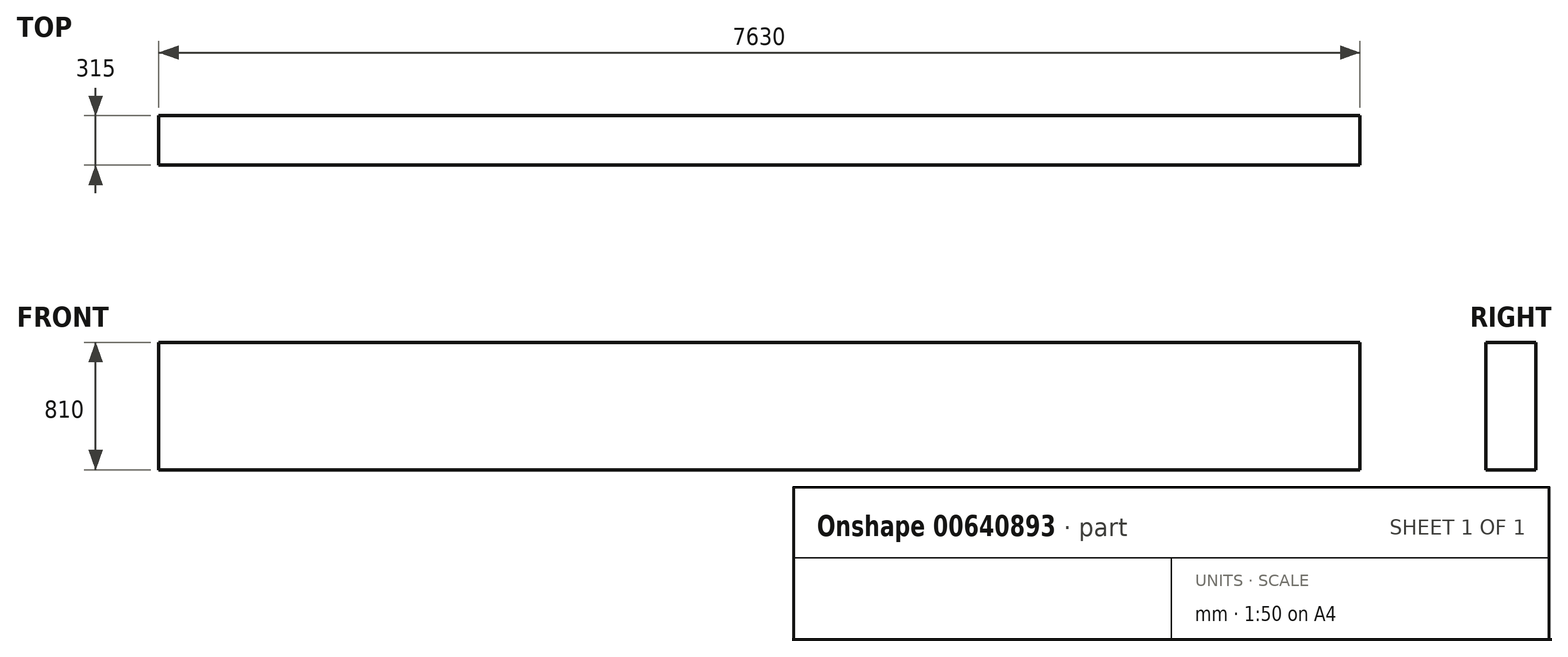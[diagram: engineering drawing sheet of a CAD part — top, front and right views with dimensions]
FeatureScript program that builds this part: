
annotation { "Feature Type Name" : "Feature", "Feature Type Description" : "" }
export const myFeature = defineFeature(function(context is Context, id is Id, definition is map)
    precondition{}
    {
        {
            var Q0;
            Q0=qCreatedBy(makeId("Top.planeOp"),FACE);
            var sketch = newSketch(context, id + "F0", { "sketchPlane" : qUnion([Q0])});
            skLineSegment(sketch, "E0.bottom", {"start": v(-3815, 157.5) * mm, "end": v(3815, 157.5) * mm});
            skLineSegment(sketch, "E0.top", {"start": v(-3815, -157.5) * mm, "end": v(3815, -157.5) * mm});
            skLineSegment(sketch, "E0.left", {"start": v(-3815, 157.5) * mm, "end": v(-3815, -157.5) * mm});
            skLineSegment(sketch, "E0.right", {"start": v(3815, 157.5) * mm, "end": v(3815, -157.5) * mm});
            skLineSegment(sketch, "E1", {"start": v(-2444.03, 0) * mm, "end": v(2309.7, 0) * mm, "construction": true});
            skLineSegment(sketch, "E2", {"start": v(0, 925.83) * mm, "end": v(0, -1040.92) * mm, "construction": true});
            skSolve(sketch);
        }
        {
            var Q0;
            Q0 = qSketchRegion(id + "F0", true);
            extrude(context, id + "F1", {"entities" : qUnion([Q0]), "depth" : 810 * mm, "offsetDistance" : 25.4 * mm});
        }
    });
